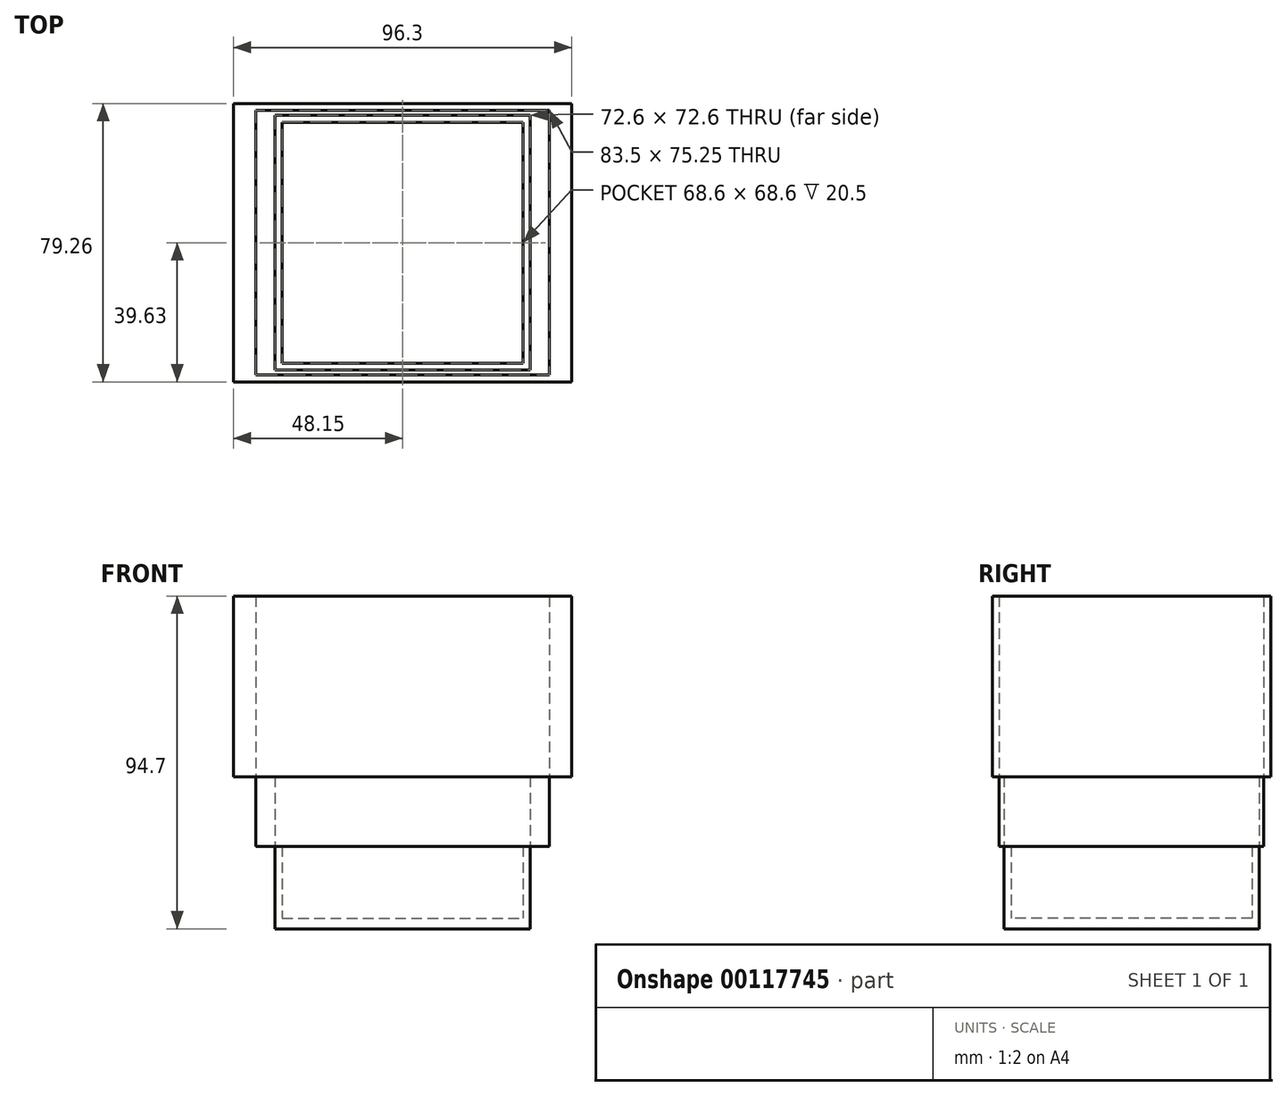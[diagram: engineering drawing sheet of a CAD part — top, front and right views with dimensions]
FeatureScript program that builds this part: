
annotation { "Feature Type Name" : "Feature", "Feature Type Description" : "" }
export const myFeature = defineFeature(function(context is Context, id is Id, definition is map)
    precondition{}
    {
        {
            var Q0;
            Q0=qCreatedBy(makeId("Top.planeOp"),FACE);
            var sketch = newSketch(context, id + "F0", { "sketchPlane" : qUnion([Q0])});
            skLineSegment(sketch, "E0.bottom", {"start": v(0, 0) * mm, "end": v(68.6, 0) * mm});
            skLineSegment(sketch, "E0.top", {"start": v(0, -68.6) * mm, "end": v(68.6, -68.6) * mm});
            skLineSegment(sketch, "E0.left", {"start": v(0, 0) * mm, "end": v(0, -68.6) * mm});
            skLineSegment(sketch, "E0.right", {"start": v(68.6, 0) * mm, "end": v(68.6, -68.6) * mm});
            skLineSegment(sketch, "E1.bottom", {"start": v(-2, 2) * mm, "end": v(70.6, 2) * mm});
            skLineSegment(sketch, "E1.top", {"start": v(-2, -70.6) * mm, "end": v(70.6, -70.6) * mm});
            skLineSegment(sketch, "E1.left", {"start": v(-2, 2) * mm, "end": v(-2, -70.6) * mm});
            skLineSegment(sketch, "E1.right", {"start": v(70.6, 2) * mm, "end": v(70.6, -70.6) * mm});
            skPoint(sketch, "E2", {"position": v(34.3, 0) * mm});
            skPoint(sketch, "E3", {"position": v(34.3, 2) * mm});
            skPoint(sketch, "E4", {"position": v(0, -34.3) * mm});
            skPoint(sketch, "E5", {"position": v(-2, -34.3) * mm});
            skSolve(sketch);
        }
        {
            var Q0;
            Q0=makeQuery(id+"F0.imprint","IMPRINT",FACE,{"disambiguationData":[TD([[makeQuery(id+"F0.imprint","IMPRINT",EDGE,{"derivedFrom":sQuery(id+"F0.wireOp",EDGE,"E0.bottom")}),-1.0]])]});
            extrude(context, id + "F1", {"entities" : qUnion([Q0]), "depth" : 3 * mm});
        }
        {
            var Q0;
            Q0=makeQuery(id+"F0.imprint","IMPRINT",FACE,{"disambiguationData":[TD([[makeQuery(id+"F0.imprint","IMPRINT",EDGE,{"derivedFrom":sQuery(id+"F0.wireOp",EDGE,"E0.bottom")}),1.0]])]});
            extrude(context, id + "F2", {"entities" : qUnion([Q0]), "operationType" : NewBodyOperationType.ADD, "depth" : 23.5 * mm});
        }
        {
            var Q0;
            Q0=makeQuery(id+"F2.opExtrude","CAP_FACE",FACE,{"disambiguationData":[OSD([sQuery(id+"F0.wireOp",EDGE,"E0.bottom"),sQuery(id+"F0.wireOp",EDGE,"E0.top"),sQuery(id+"F0.wireOp",EDGE,"E0.left"),sQuery(id+"F0.wireOp",EDGE,"E0.right"),sQuery(id+"F0.wireOp",EDGE,"E1.bottom"),sQuery(id+"F0.wireOp",EDGE,"E1.top"),sQuery(id+"F0.wireOp",EDGE,"E1.left"),sQuery(id+"F0.wireOp",EDGE,"E1.right")])],"isStart":false});
            var sketch = newSketch(context, id + "F3", { "sketchPlane" : qUnion([Q0])});
            skLineSegment(sketch, "E6.bottom", {"start": v(-7.45, 3.33) * mm, "end": v(76.05, 3.33) * mm});
            skLineSegment(sketch, "E6.top", {"start": v(-7.45, -71.92) * mm, "end": v(76.05, -71.92) * mm});
            skLineSegment(sketch, "E6.left", {"start": v(-7.45, 3.33) * mm, "end": v(-7.45, -71.92) * mm});
            skLineSegment(sketch, "E6.right", {"start": v(76.05, 3.33) * mm, "end": v(76.05, -71.92) * mm});
            skPoint(sketch, "E7", {"position": v(34.3, 3.33) * mm});
            skPoint(sketch, "E8", {"position": v(-7.45, -34.3) * mm});
            skPoint(sketch, "E9", {"position": v(34.3, 2) * mm});
            skPoint(sketch, "E10", {"position": v(-2, -34.3) * mm});
            skLineSegment(sketch, "E11.bottom", {"start": v(-9.45, 5.33) * mm, "end": v(78.05, 5.33) * mm});
            skLineSegment(sketch, "E11.top", {"start": v(-9.45, -75.92) * mm, "end": v(78.05, -75.92) * mm});
            skLineSegment(sketch, "E11.left", {"start": v(-9.45, 5.33) * mm, "end": v(-9.45, -75.92) * mm});
            skLineSegment(sketch, "E11.right", {"start": v(78.05, 5.33) * mm, "end": v(78.05, -75.92) * mm});
            skSolve(sketch);
        }
        {
            var Q0;
            Q0=makeQuery(id+"F3.imprint","IMPRINT",FACE,{"disambiguationData":[TD([[makeQuery(id+"F3.imprint","IMPRINT",EDGE,{"derivedFrom":sQuery(id+"F3.wireOp",EDGE,"E6.bottom")}),-1.0]])]});
            extrude(context, id + "F4", {"entities" : qUnion([Q0]), "depth" : 19.8 * mm});
        }
        {
            var Q0;
            Q0=makeQuery(id+"F4.opExtrude","CAP_FACE",FACE,{"disambiguationData":[OSD([sQuery(id+"F0.wireOp",EDGE,"E1.bottom"),sQuery(id+"F0.wireOp",EDGE,"E1.top"),sQuery(id+"F0.wireOp",EDGE,"E1.left"),sQuery(id+"F0.wireOp",EDGE,"E1.right"),sQuery(id+"F3.wireOp",EDGE,"E6.bottom"),sQuery(id+"F3.wireOp",EDGE,"E6.top"),sQuery(id+"F3.wireOp",EDGE,"E6.left"),sQuery(id+"F3.wireOp",EDGE,"E6.right")])],"isStart":false});
            var sketch = newSketch(context, id + "F5", { "sketchPlane" : qUnion([Q0])});
            skLineSegment(sketch, "E12.bottom", {"start": v(-13.85, 5.32) * mm, "end": v(82.45, 5.32) * mm});
            skLineSegment(sketch, "E12.top", {"start": v(-13.85, -73.92) * mm, "end": v(82.45, -73.92) * mm});
            skLineSegment(sketch, "E12.left", {"start": v(-13.85, 5.32) * mm, "end": v(-13.85, -73.92) * mm});
            skLineSegment(sketch, "E12.right", {"start": v(82.45, 5.32) * mm, "end": v(82.45, -73.92) * mm});
            skPoint(sketch, "E13", {"position": v(34.3, 5.32) * mm});
            skPoint(sketch, "E14", {"position": v(-13.85, -34.3) * mm});
            skPoint(sketch, "E15", {"position": v(34.3, 3.33) * mm});
            skPoint(sketch, "E16", {"position": v(-7.45, -34.3) * mm});
            skSolve(sketch);
        }
        {
            var Q0;
            Q0=makeQuery(id+"F5.imprint","IMPRINT",FACE,{"disambiguationData":[TD([[makeQuery(id+"F5.imprint","IMPRINT",EDGE,{"derivedFrom":sQuery(id+"F5.wireOp",EDGE,"E12.bottom")}),-1.0]])]});
            extrude(context, id + "F6", {"entities" : qUnion([Q0]), "depth" : 51.4 * mm});
        }
    });
